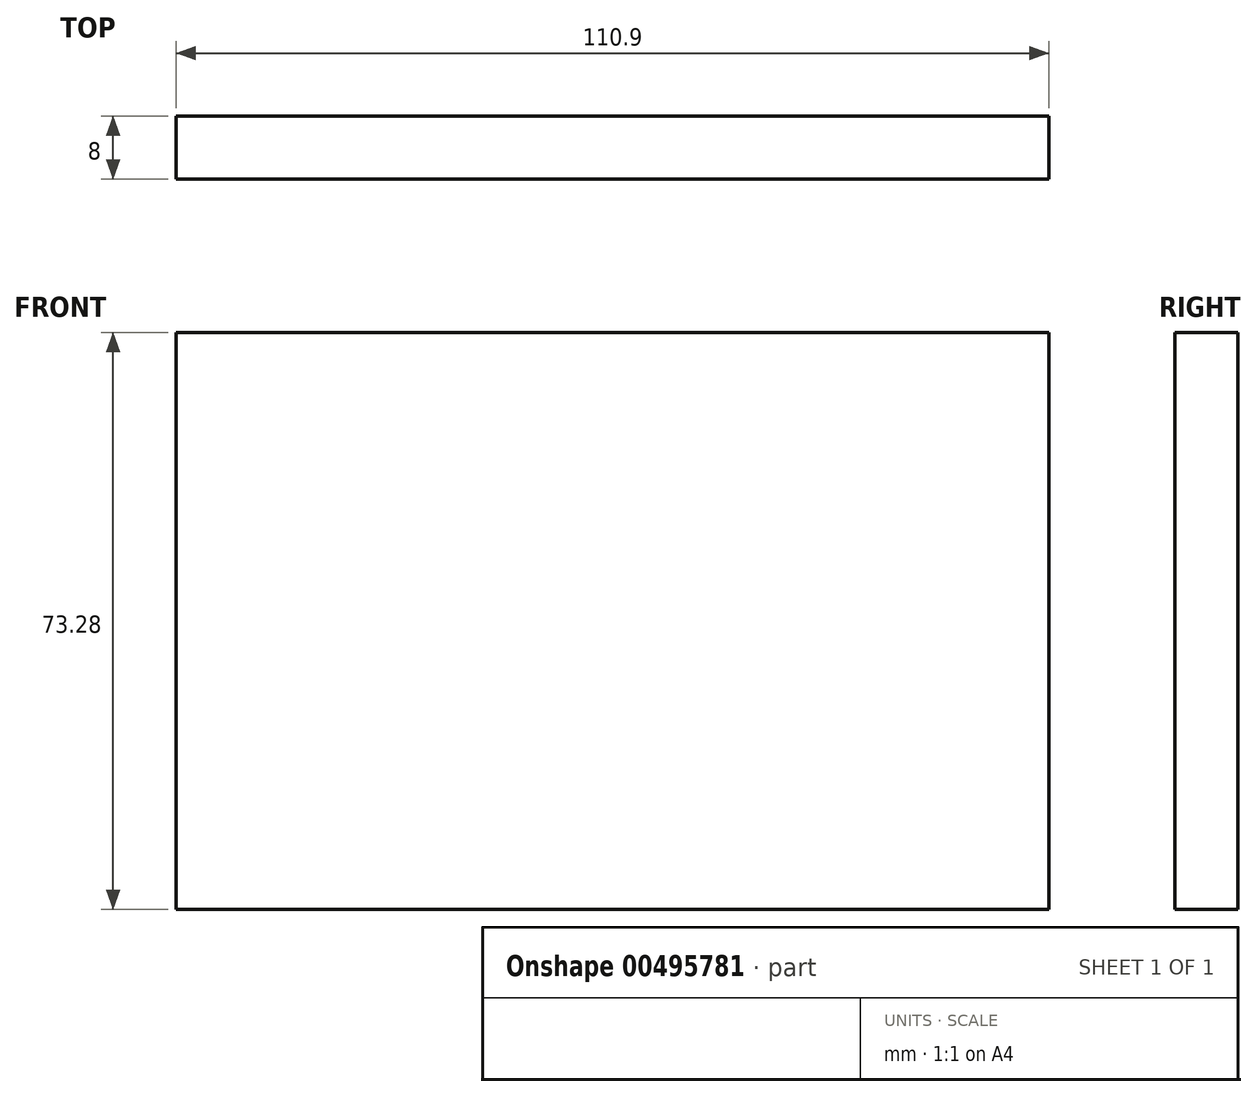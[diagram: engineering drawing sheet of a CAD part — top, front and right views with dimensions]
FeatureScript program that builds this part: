
annotation { "Feature Type Name" : "Feature", "Feature Type Description" : "" }
export const myFeature = defineFeature(function(context is Context, id is Id, definition is map)
    precondition{}
    {
        {
            var Q0;
            Q0=qCreatedBy(makeId("Front.planeOp"),FACE);
            var sketch = newSketch(context, id + "F0", { "sketchPlane" : qUnion([Q0])});
            skLineSegment(sketch, "E0.bottom", {"start": v(-55.25, 48.52) * mm, "end": v(55.65, 48.52) * mm});
            skLineSegment(sketch, "E0.top", {"start": v(-55.25, -24.76) * mm, "end": v(55.65, -24.76) * mm});
            skLineSegment(sketch, "E0.left", {"start": v(-55.25, 48.52) * mm, "end": v(-55.25, -24.76) * mm});
            skLineSegment(sketch, "E0.right", {"start": v(55.65, 48.52) * mm, "end": v(55.65, -24.76) * mm});
            skSolve(sketch);
        }
        {
            var Q0;
            Q0=makeQuery(id+"F0.imprint","IMPRINT",FACE,{"disambiguationData":[TD([[makeQuery(id+"F0.imprint","IMPRINT",EDGE,{"derivedFrom":sQuery(id+"F0.wireOp",EDGE,"E0.bottom")}),-1.0]])]});
            extrude(context, id + "F1", {"entities" : qUnion([Q0]), "endBound" : BoundingType.SYMMETRIC, "depth" : 8 * mm, "offsetDistance" : 25 * mm});
        }
    });
